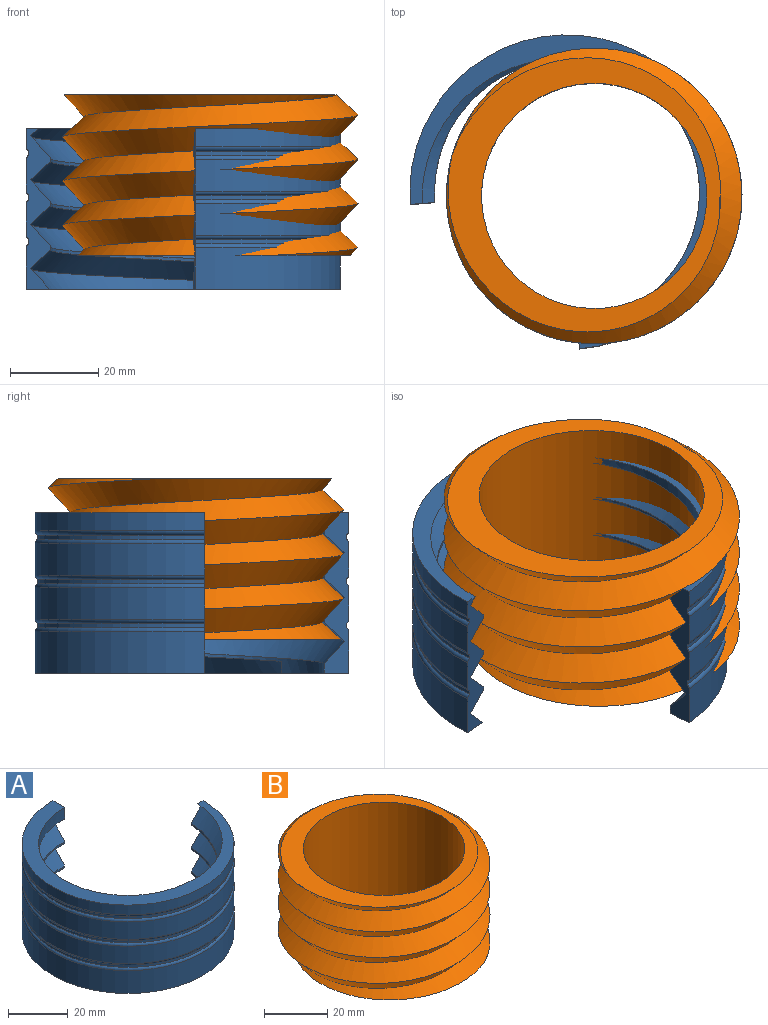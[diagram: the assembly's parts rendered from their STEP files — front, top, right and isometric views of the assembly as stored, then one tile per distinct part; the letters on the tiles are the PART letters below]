
ASSEMBLY  parts=2 mates=1
PART A: 30 faces, bbox 80.4x80.4x48.8 mm
  f0: cylinder r=30mm len=60mm, axis (0,0,-1), area 99.9mm2, adj f6,f10,f28,f29
  f1: cylinder r=30mm len=60mm, axis (0,0,-1), area 99.9mm2, adj f5,f9,f28,f29
  f2: cylinder r=30mm len=60mm, axis (0,0,-1), area 147mm2, adj f3,f4,f8,f18,f28,f29
  f3: plane 74.58x74.58mm, normal (0,0,-1), area 516.9mm2, adj f2,f7,f8,f12,f18,f28,f29
  f4: bspline ~69.26x69.26mm, area 1044.8mm2, adj f2,f9,f28,f29
  f5: bspline ~69.26x69.26mm, area 1044.8mm2, adj f1,f10,f28,f29
  f6: bspline ~69.26x69.26mm, area 1044.8mm2, adj f0,f11,f28,f29
  f7: bspline ~69.26x59.11mm, area 318.6mm2, adj f3,f8,f28
  f8: bspline ~69.26x69.26mm, area 764.7mm2, adj f2,f3,f7,f18,f28
  f9: bspline ~69.26x69.26mm, area 955.7mm2, adj f1,f4,f28,f29
  f10: bspline ~69.26x69.26mm, area 955.7mm2, adj f0,f5,f28,f29
  f11: bspline ~69.26x69.26mm, area 851.6mm2, adj f6,f15,f16,f28,f29
  f12: cylinder r=35.6mm len=71.2mm, axis (0,0,-1), area 1574.2mm2, adj f3,f23,f28,f29
  f13: cylinder r=35.6mm len=71.2mm, axis (0,0,-1), area 1202.3mm2, adj f22,f25,f28,f29
  f14: cylinder r=35.6mm len=71.2mm, axis (0,0,-1), area 1202.3mm2, adj f24,f27,f28,f29
  f15: cylinder r=30mm len=59.78mm, axis (0,0,-1), area 218.1mm2, adj f11,f16,f29
  f16: plane 71.2x71.2mm, normal (0,0,1), area 788.7mm2, adj f11,f15,f17,f28,f29
  f17: cylinder r=35.6mm len=71.2mm, axis (0,0,-1), area 685mm2, adj f16,f26,f28,f29
  f18: plane 2.69x2.15mm, normal (-0.73,-0.68,0), area 3.9mm2, adj f2,f3,f8
  f19: cylinder r=35mm len=70mm, axis (0,0,1), area 164.9mm2, adj f26,f27,f28,f29
  f20: cylinder r=35mm len=70mm, axis (0,0,1), area 164.9mm2, adj f24,f25,f28,f29
  f21: cylinder r=35mm len=70mm, axis (0,0,1), area 164.9mm2, adj f22,f23,f28,f29
  f22: torus R=34.6mm, axis (0,0,-1), area 193.3mm2, adj f13,f21,f28,f29
  f23: torus R=34.6mm, axis (0,0,1), area 193.3mm2, adj f12,f21,f28,f29
  f24: torus R=34.6mm, axis (0,0,-1), area 193.3mm2, adj f14,f20,f28,f29
  f25: torus R=34.6mm, axis (0,0,1), area 193.3mm2, adj f13,f20,f28,f29
  f26: torus R=34.6mm, axis (0,0,-1), area 193.3mm2, adj f17,f19,f28,f29
  f27: torus R=34.6mm, axis (0,0,1), area 193.3mm2, adj f14,f19,f28,f29
  f28: plane 36.3x5.6mm, normal (0,1,0), area 118.5mm2, adj f0,f1,f2,f3,f4,f5,f6,f7
  f29: plane 36.3x5.6mm, normal (1,0,0), area 136mm2, adj f0,f1,f2,f3,f4,f5,f6,f9
PART B: 5 faces, bbox 67.4x67.4x47.9 mm
  f0: bspline ~67.43x67.43mm, area 4772.6mm2, adj f1,f2,f3
  f1: bspline ~67.43x67.43mm, area 5216.8mm2, adj f0,f2,f3
  f2: plane 62.11x61.66mm, normal (0,0,1), area 980.5mm2, adj f0,f1,f4
  f3: plane 62.33x61.89mm, normal (0,0,-1), area 980.5mm2, adj f0,f1,f4
  f4: cylinder r=25.5mm len=51mm, axis (0,0,-1), area 5816mm2, adj f2,f3
PLACE A rot(axis=(0,0,-1),175.5deg) t=(-2.11,96.55,-5.53)mm
PLACE B t=(4.03,95.66,2.21)mm fixed
MATE cylindrical B.f2 <-> A.f0  axis (0,0,1) through (-2.11,96.55,38.51)mm
